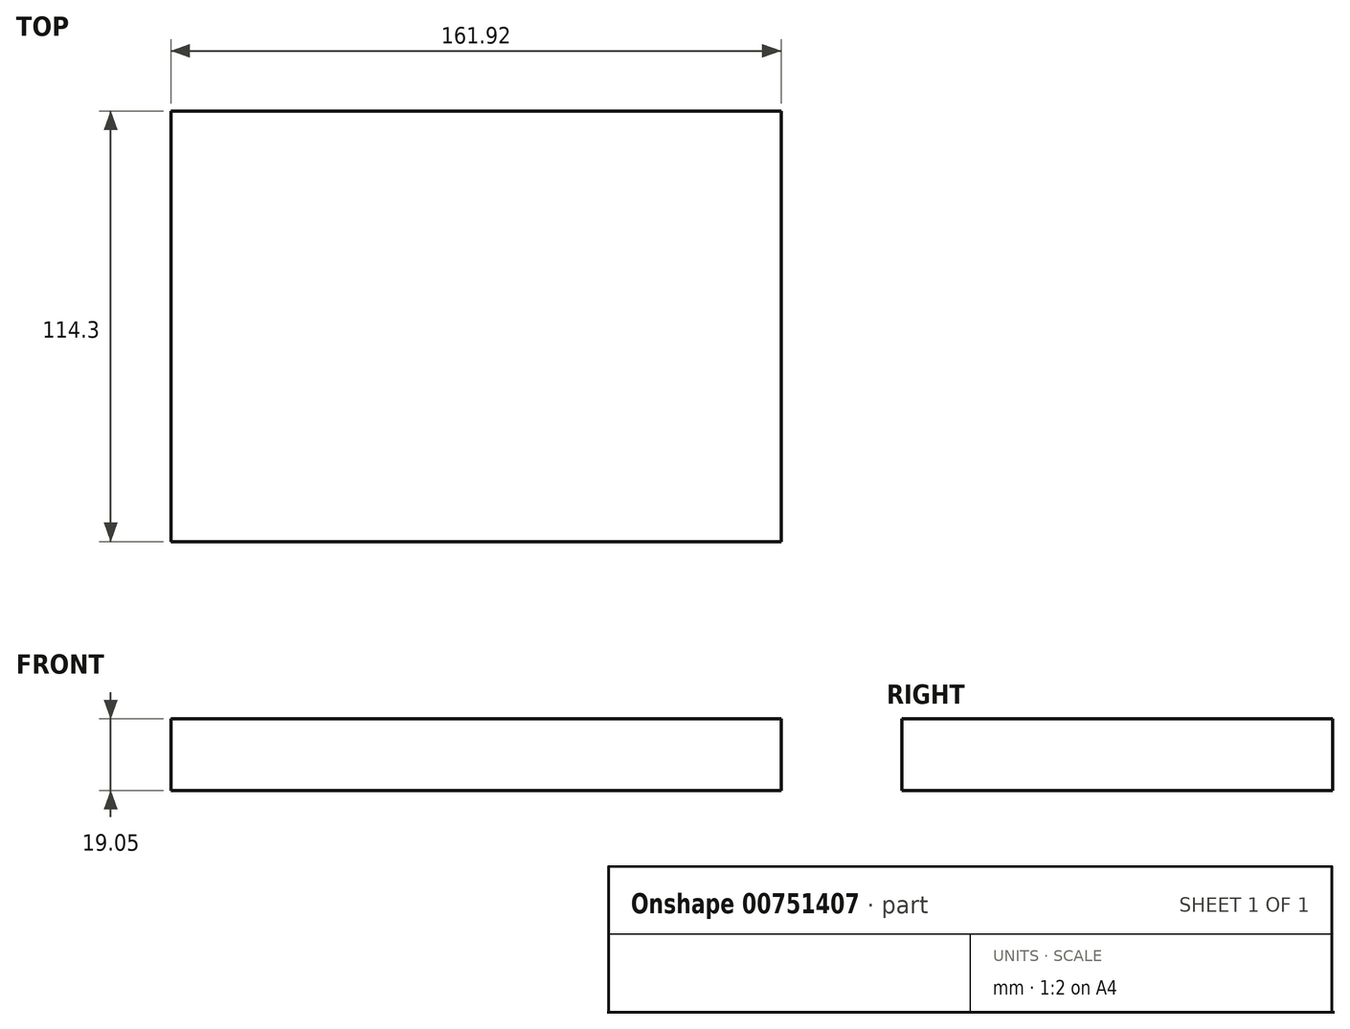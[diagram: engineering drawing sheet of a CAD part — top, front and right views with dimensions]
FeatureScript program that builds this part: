
annotation { "Feature Type Name" : "Feature", "Feature Type Description" : "" }
export const myFeature = defineFeature(function(context is Context, id is Id, definition is map)
    precondition{}
    {
        {
            var Q0;
            Q0=qCreatedBy(makeId("Top.planeOp"),FACE);
            var sketch = newSketch(context, id + "F0", { "sketchPlane" : qUnion([Q0])});
            skLineSegment(sketch, "E0.bottom", {"start": v(-80.96, 57.15) * mm, "end": v(80.96, 57.15) * mm});
            skLineSegment(sketch, "E0.top", {"start": v(-80.96, -57.15) * mm, "end": v(80.96, -57.15) * mm});
            skLineSegment(sketch, "E0.left", {"start": v(-80.96, 57.15) * mm, "end": v(-80.96, -57.15) * mm});
            skLineSegment(sketch, "E0.right", {"start": v(80.96, 57.15) * mm, "end": v(80.96, -57.15) * mm});
            skLineSegment(sketch, "E1", {"start": v(80.96, 57.15) * mm, "end": v(-80.96, -57.15) * mm, "construction": true});
            skPoint(sketch, "E2", {"position": v(0, 0) * mm});
            skLineSegment(sketch, "E3", {"start": v(-80.96, 57.15) * mm, "end": v(80.96, -57.15) * mm, "construction": true});
            skSolve(sketch);
        }
        {
            var Q0;
            Q0=makeQuery(id+"F0.imprint","IMPRINT",FACE,{"disambiguationData":[TD([[makeQuery(id+"F0.imprint","IMPRINT",EDGE,{"derivedFrom":sQuery(id+"F0.wireOp",EDGE,"E0.bottom")}),-1.0]])]});
            extrude(context, id + "F1", {"entities" : qUnion([Q0]), "depth" : 19.05 * mm, "offsetDistance" : 25.4 * mm});
        }
    });
